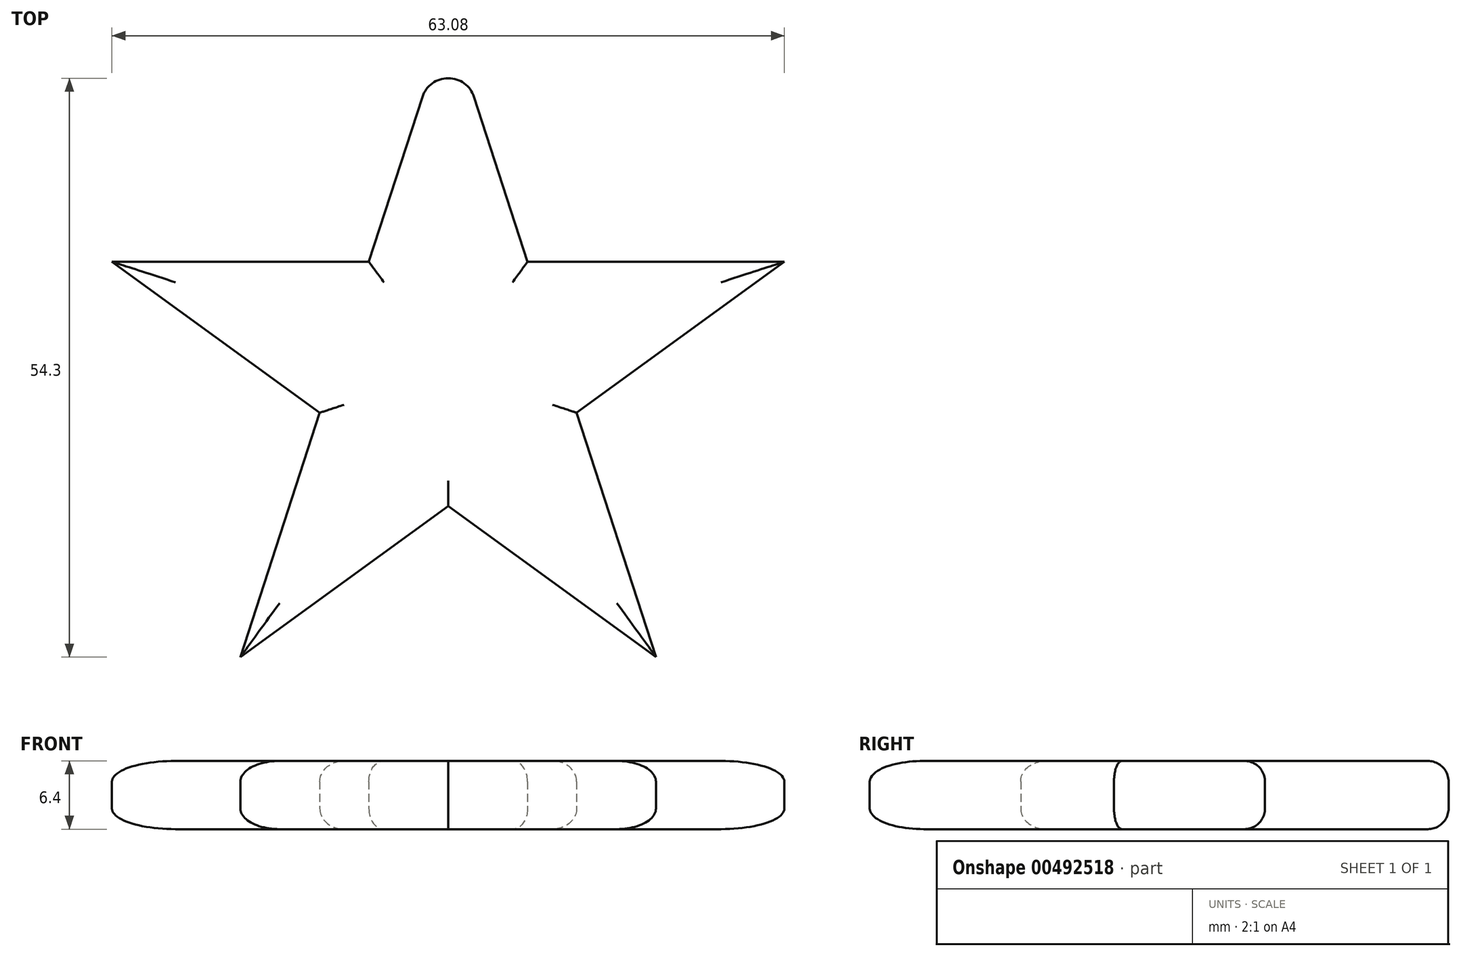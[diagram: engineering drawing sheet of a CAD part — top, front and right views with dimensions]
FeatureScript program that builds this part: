
annotation { "Feature Type Name" : "Feature", "Feature Type Description" : "" }
export const myFeature = defineFeature(function(context is Context, id is Id, definition is map)
    precondition{}
    {
        {
            var Q0;
            Q0=qCreatedBy(makeId("Top.planeOp"),FACE);
            var sketch = newSketch(context, id + "F0", { "sketchPlane" : qUnion([Q0])});
            skLineSegment(sketch, "E0.MirrorCS", {"start": v(12.05, -39.93) * mm, "end": v(7.45, -25.76) * mm, "construction": true});
            skLineSegment(sketch, "E1.MirrorCS", {"start": v(7.45, -25.76) * mm, "end": v(-7.45, -25.76) * mm, "construction": true});
            skLineSegment(sketch, "E2.MirrorCS", {"start": v(-12.05, -39.93) * mm, "end": v(-19.5, -62.85) * mm});
            skLineSegment(sketch, "E3.MirrorCS", {"start": v(-7.45, -25.76) * mm, "end": v(0, -2.85) * mm});
            skLineSegment(sketch, "E4.MirrorCS", {"start": v(31.54, -25.76) * mm, "end": v(7.45, -25.76) * mm});
            skLineSegment(sketch, "E5.MirrorCS", {"start": v(12.05, -39.93) * mm, "end": v(31.54, -25.76) * mm});
            skLineSegment(sketch, "E6.MirrorCS", {"start": v(12.05, -39.93) * mm, "end": v(19.5, -62.85) * mm});
            skLineSegment(sketch, "E7.MirrorCS", {"start": v(19.5, -62.85) * mm, "end": v(0, -48.68) * mm});
            skLineSegment(sketch, "E8.MirrorCS", {"start": v(-31.54, -25.76) * mm, "end": v(-12.05, -39.93) * mm});
            skLineSegment(sketch, "E9.MirrorCS", {"start": v(-7.45, -25.76) * mm, "end": v(-31.54, -25.76) * mm});
            skPoint(sketch, "E10.MirrorP", {"position": v(0, -36.01) * mm});
            skLineSegment(sketch, "E11.MirrorCS", {"start": v(0, -2.85) * mm, "end": v(7.45, -25.76) * mm});
            skLineSegment(sketch, "E12.MirrorCS", {"start": v(-7.45, -25.76) * mm, "end": v(-12.05, -39.93) * mm, "construction": true});
            skLineSegment(sketch, "E13.MirrorCS", {"start": v(-19.5, -62.85) * mm, "end": v(0, -48.68) * mm});
            skLineSegment(sketch, "E14.MirrorCS", {"start": v(-12.05, -39.93) * mm, "end": v(0, -48.68) * mm, "construction": true});
            skLineSegment(sketch, "E15.MirrorCS", {"start": v(0, -48.68) * mm, "end": v(12.05, -39.93) * mm, "construction": true});
            skPoint(sketch, "E16.MirrorP", {"position": v(9.75, -32.85) * mm});
            skSolve(sketch);
        }
        {
            var Q0;
            Q0=makeQuery(id+"F0.imprint","IMPRINT",FACE,{"disambiguationData":[TD([[makeQuery(id+"F0.imprint","IMPRINT",EDGE,{"derivedFrom":sQuery(id+"F0.wireOp",EDGE,"E2.MirrorCS")}),1.0]])]});
            extrude(context, id + "F1", {"entities" : qUnion([Q0]), "depth" : 6.4 * mm});
        }
        {
            var Q0;
            Q0=makeQuery(id+"F1.opExtrude","CAP_FACE",FACE,{"disambiguationData":[OSD([sQuery(id+"F0.wireOp",EDGE,"E2.MirrorCS"),sQuery(id+"F0.wireOp",EDGE,"E3.MirrorCS"),sQuery(id+"F0.wireOp",EDGE,"E4.MirrorCS"),sQuery(id+"F0.wireOp",EDGE,"E5.MirrorCS"),sQuery(id+"F0.wireOp",EDGE,"E6.MirrorCS"),sQuery(id+"F0.wireOp",EDGE,"E7.MirrorCS"),sQuery(id+"F0.wireOp",EDGE,"E8.MirrorCS"),sQuery(id+"F0.wireOp",EDGE,"E9.MirrorCS"),sQuery(id+"F0.wireOp",EDGE,"E11.MirrorCS"),sQuery(id+"F0.wireOp",EDGE,"E13.MirrorCS")])],"isStart":false});
            var sketch = newSketch(context, id + "F2", { "sketchPlane" : qUnion([Q0])});
            skLineSegment(sketch, "E17", {"start": v(7.45, -25.76) * mm, "end": v(12.05, -39.93) * mm});
            skLineSegment(sketch, "E18", {"start": v(31.54, -25.76) * mm, "end": v(9.75, -32.85) * mm});
            skPoint(sketch, "E19", {"position": v(15.25, -31.06) * mm});
            skSolve(sketch);
        }
        {
            var Q0;
            Q0=sQuery(id+"F2.wireOp",EDGE,"E18");
            cPlane(context, id + "F3", {"entities" : qUnion([Q0]), "cplaneType" : CPlaneType.LINE_ANGLE, "offset" : 25 * mm, "angle" : 0 * degree, "width" : 150 * mm, "height" : 150 * mm});
        }
        {
            var Q0;
            Q0=qCreatedBy(id+"F3.planeOp",FACE);
            var sketch = newSketch(context, id + "F4", { "sketchPlane" : qUnion([Q0])});
            skLineSegment(sketch, "E20", {"start": v(4.9, 6.4) * mm, "end": v(5.9, 6.4) * mm});
            skArc(sketch, "E21", {"start": v(5.9, 6.4) * mm, "mid": v(5.61, 7.1) * mm, "end": v(4.9, 7.4) * mm});
            skLineSegment(sketch, "E22", {"start": v(4.9, 6.4) * mm, "end": v(4.9, 7.4) * mm});
            skSolve(sketch);
        }
        {
            var Q0;
            Q0=makeQuery(id+"F1.opExtrude","CAP_EDGE",EDGE,{"disambiguationData":[OSD([sQuery(id+"F0.wireOp",EDGE,"E8.MirrorCS")])],"isStart":false});
            var Q1;
            Q1=makeQuery(id+"F1.opExtrude","CAP_EDGE",EDGE,{"disambiguationData":[OSD([sQuery(id+"F0.wireOp",EDGE,"E2.MirrorCS")])],"isStart":false});
            var Q2;
            Q2=makeQuery(id+"F1.opExtrude","CAP_EDGE",EDGE,{"disambiguationData":[OSD([sQuery(id+"F0.wireOp",EDGE,"E13.MirrorCS")])],"isStart":false});
            var Q3;
            Q3=makeQuery(id+"F1.opExtrude","CAP_EDGE",EDGE,{"disambiguationData":[OSD([sQuery(id+"F0.wireOp",EDGE,"E7.MirrorCS")])],"isStart":false});
            var Q4;
            Q4=makeQuery(id+"F1.opExtrude","CAP_EDGE",EDGE,{"disambiguationData":[OSD([sQuery(id+"F0.wireOp",EDGE,"E6.MirrorCS")])],"isStart":false});
            var Q5;
            Q5=makeQuery(id+"F1.opExtrude","CAP_EDGE",EDGE,{"disambiguationData":[OSD([sQuery(id+"F0.wireOp",EDGE,"E5.MirrorCS")])],"isStart":false});
            var Q6;
            Q6=makeQuery(id+"F1.opExtrude","CAP_EDGE",EDGE,{"disambiguationData":[OSD([sQuery(id+"F0.wireOp",EDGE,"E4.MirrorCS")])],"isStart":false});
            var Q7;
            Q7=makeQuery(id+"F1.opExtrude","CAP_EDGE",EDGE,{"disambiguationData":[OSD([sQuery(id+"F0.wireOp",EDGE,"E11.MirrorCS")])],"isStart":false});
            var Q8;
            Q8=makeQuery(id+"F1.opExtrude","CAP_EDGE",EDGE,{"disambiguationData":[OSD([sQuery(id+"F0.wireOp",EDGE,"E3.MirrorCS")])],"isStart":false});
            var Q9;
            Q9=makeQuery(id+"F1.opExtrude","CAP_EDGE",EDGE,{"disambiguationData":[OSD([sQuery(id+"F0.wireOp",EDGE,"E9.MirrorCS")])],"isStart":false});
            var Q10;
            Q10=makeQuery(id+"F1.opExtrude","CAP_EDGE",EDGE,{"disambiguationData":[OSD([sQuery(id+"F0.wireOp",EDGE,"E8.MirrorCS")])],"isStart":true});
            var Q11;
            Q11=makeQuery(id+"F1.opExtrude","CAP_EDGE",EDGE,{"disambiguationData":[OSD([sQuery(id+"F0.wireOp",EDGE,"E2.MirrorCS")])],"isStart":true});
            var Q12;
            Q12=makeQuery(id+"F1.opExtrude","CAP_EDGE",EDGE,{"disambiguationData":[OSD([sQuery(id+"F0.wireOp",EDGE,"E13.MirrorCS")])],"isStart":true});
            var Q13;
            Q13=makeQuery(id+"F1.opExtrude","CAP_EDGE",EDGE,{"disambiguationData":[OSD([sQuery(id+"F0.wireOp",EDGE,"E7.MirrorCS")])],"isStart":true});
            var Q14;
            Q14=makeQuery(id+"F1.opExtrude","CAP_EDGE",EDGE,{"disambiguationData":[OSD([sQuery(id+"F0.wireOp",EDGE,"E6.MirrorCS")])],"isStart":true});
            var Q15;
            Q15=makeQuery(id+"F1.opExtrude","CAP_EDGE",EDGE,{"disambiguationData":[OSD([sQuery(id+"F0.wireOp",EDGE,"E5.MirrorCS")])],"isStart":true});
            var Q16;
            Q16=makeQuery(id+"F1.opExtrude","CAP_EDGE",EDGE,{"disambiguationData":[OSD([sQuery(id+"F0.wireOp",EDGE,"E4.MirrorCS")])],"isStart":true});
            var Q17;
            Q17=makeQuery(id+"F1.opExtrude","CAP_EDGE",EDGE,{"disambiguationData":[OSD([sQuery(id+"F0.wireOp",EDGE,"E11.MirrorCS")])],"isStart":true});
            var Q18;
            Q18=makeQuery(id+"F1.opExtrude","CAP_EDGE",EDGE,{"disambiguationData":[OSD([sQuery(id+"F0.wireOp",EDGE,"E3.MirrorCS")])],"isStart":true});
            var Q19;
            Q19=makeQuery(id+"F1.opExtrude","CAP_EDGE",EDGE,{"disambiguationData":[OSD([sQuery(id+"F0.wireOp",EDGE,"E9.MirrorCS")])],"isStart":true});
            fillet(context, id + "F5", {"entities" : qUnion([Q0, Q1, Q2, Q3, Q4, Q5, Q6, Q7, Q8, Q9, Q10, Q11, Q12, Q13, Q14, Q15, Q16, Q17, Q18, Q19]), "radius" : 1.93 * mm, "tangentPropagation" : true, "allowEdgeOverflow" : false});
        }
        {
            var Q0;
            Q0=makeQuery(id+"F1.opExtrude","SWEPT_EDGE",EDGE,{"disambiguationData":[OSD([sQuery(id+"F0.wireOp",EDGE,"E3.MirrorCS"),sQuery(id+"F0.wireOp",EDGE,"E11.MirrorCS")])]});
            fillet(context, id + "F6", {"entities" : qUnion([Q0]), "radius" : 2.55 * mm, "tangentPropagation" : true, "allowEdgeOverflow" : false});
        }
    });
